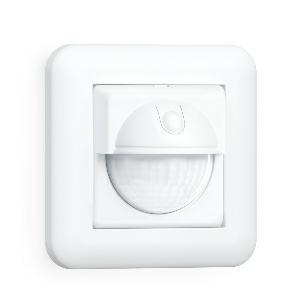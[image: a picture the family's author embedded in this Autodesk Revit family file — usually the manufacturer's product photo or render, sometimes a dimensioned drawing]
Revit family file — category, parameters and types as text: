
# Revit family: ir_2180_up_eco_065003
name_source: partatom
category: Elektroinstallationen
revit_build: Autodesk Revit 2016 (Build: 20190508_0715(x64)
units: mm (PartAtom-declared; Revit-internal decimal feet)

## family parameters
Basisbauteil = Fläche
Beim Laden mit Abzugskörper schneiden = Nein
Bemaßung runder Anschluss = Durchmesser verwenden
Beschriftungsausrichtung beibehalten = Nein
Gemeinsam genutzt = Nein
Raumberechnungspunkt = Nein
Teiletyp = Normal

## types (1)
- IR 2180 UP ECO
    Apparent Load = 0 VA
    Beschreibung = Type: Motion detectors; Dimensions (L x W x H): 57 x 81 x 81 mm; Mains power supply: 220 – 240 V / 50 – 60 Hz; Sensor Technology: passive infrared; Application, place: Indoors; Application, room: corridor / aisle, function room / ancillary room, kitchenette, stairwell, WC / washroom, Indoors; Installation site: wall; Installation: Concealed wiring; Electronic scalability: No; Mechanical scalability: No; Mounting height: 1,10 – 2,2 m; Optimum mounting height: 1,1 m; Detection angle: 180 °; Angle of aperture: 90 °; Sneak-by guard: Yes; Reach, radial: r = 2 m (6 m²); Reach, tangential: r = 8 m (101 m²); Twilight setting TEACH: No; Twilight setting: 2 – 1000 lx; Time setting: 5 sec – 30 min; Constant-lighting control: No; Basic light level function: No; Settings via: Potentiometers; With remote control: No; Interconnection: No; IP-rating: IP20; Material: Plastic; Ambient temperature: 0 – 40 °C; Colour: white; Colour, RAL: 9010; IDs, certificates: VDE; Manufacturer's Warranty: 5 years; PU1, EAN: 4007841065003
    Height = 81 mm
    Hersteller = Steinel
    Length = 57 mm
    ModVariant = Nein
    Modell = 065003
    Mounting Type = Recessed
    Number of Poles = 1
    OnlyDefault = Ja
    Power Factor = 1
    Product Name = IR 2180 UP ECO
    Product group = Sensor-switched indoor light
    ProductGroupID = 30
    Protection Class = Protection class
    Protection Degree = IP 20
    RlxData = <blob elided: 31121 chars, md5=04ca3253>
    SensorDataFile = {"IESDataFiles":[]}
    Typenbild = produkt1_065003.jpg
    Typenkommentare = Product without accessories
    URL = http://relux.com
    VarID = ---
    Voltage = 0 V
    Vorgabe-Ansicht = 1800 mm
    Weight = 0.00 kg
    Width = 81 mm

## geometry (parser evidence)
native form markers: Sweep x8
no freeform markers — native parametric forms only
